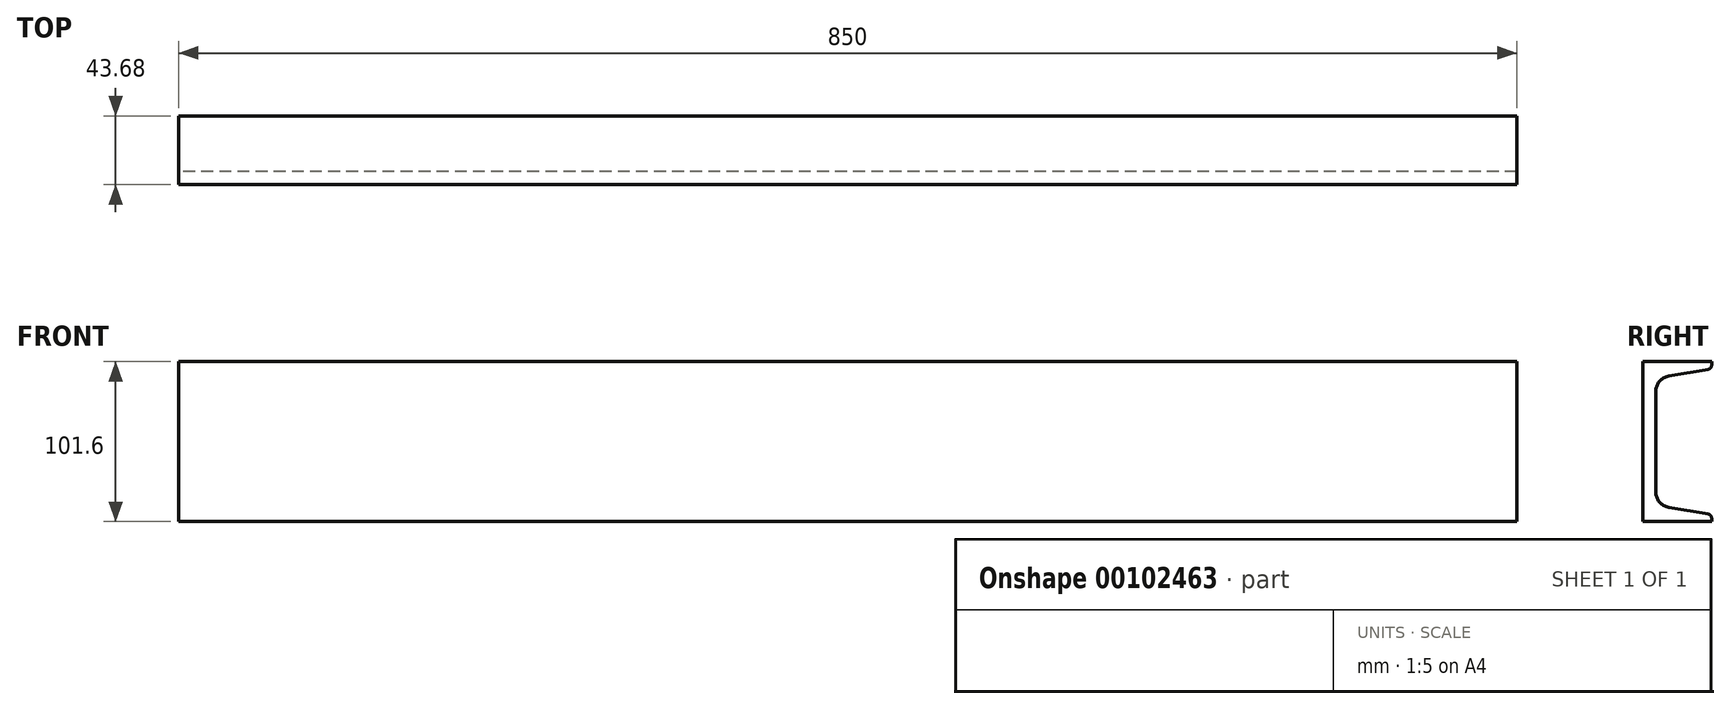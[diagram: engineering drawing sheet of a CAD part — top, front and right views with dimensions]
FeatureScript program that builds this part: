
annotation { "Feature Type Name" : "Feature", "Feature Type Description" : "" }
export const myFeature = defineFeature(function(context is Context, id is Id, definition is map)
    precondition{}
    {
        {
            var Q0;
            Q0=qCreatedBy(makeId("Right.planeOp"),FACE);
            var sketch = newSketch(context, id + "F0", { "sketchPlane" : qUnion([Q0])});
            skLineSegment(sketch, "E0", {"start": v(21.84, 50.8) * mm, "end": v(21.84, 48.6) * mm});
            skArc(sketch, "E1", {"start": v(21.84, 48.6) * mm, "mid": v(21.23, 46.93) * mm, "end": v(19.68, 46.03) * mm});
            skArc(sketch, "E2", {"start": v(-5.42, 41.6) * mm, "mid": v(-11.35, 38.18) * mm, "end": v(-13.7, 31.75) * mm, "construction": true});
            skArc(sketch, "E3", {"start": v(-13.7, -31.75) * mm, "mid": v(-11.35, -38.18) * mm, "end": v(-5.42, -41.6) * mm, "construction": true});
            skArc(sketch, "E4", {"start": v(19.68, -46.03) * mm, "mid": v(21.23, -46.93) * mm, "end": v(21.84, -48.6) * mm, "construction": true});
            skLineSegment(sketch, "E5", {"start": v(-21.84, 50.8) * mm, "end": v(21.84, 50.8) * mm});
            skLineSegment(sketch, "E6", {"start": v(-21.84, 50.8) * mm, "end": v(-21.84, -50.8) * mm});
            skLineSegment(sketch, "E7", {"start": v(-21.84, -50.8) * mm, "end": v(21.84, -50.8) * mm});
            skLineSegment(sketch, "E8", {"start": v(21.84, -50.8) * mm, "end": v(21.84, -48.6) * mm});
            skArc(sketch, "E9", {"start": v(21.84, -48.6) * mm, "mid": v(21.23, -46.93) * mm, "end": v(19.68, -46.03) * mm});
            skLineSegment(sketch, "E10", {"start": v(19.68, -46.03) * mm, "end": v(-5.42, -41.6) * mm});
            skArc(sketch, "E11", {"start": v(-5.42, -41.6) * mm, "mid": v(-11.35, -38.18) * mm, "end": v(-13.7, -31.75) * mm, "construction": true});
            skLineSegment(sketch, "E12", {"start": v(-13.7, -31.75) * mm, "end": v(-13.7, 31.75) * mm});
            skArc(sketch, "E13", {"start": v(-5.42, -41.6) * mm, "mid": v(-11.35, -38.18) * mm, "end": v(-13.7, -31.75) * mm});
            skArc(sketch, "E14", {"start": v(-13.7, 31.75) * mm, "mid": v(-11.35, 38.18) * mm, "end": v(-5.42, 41.6) * mm});
            skLineSegment(sketch, "E15", {"start": v(-5.42, 41.6) * mm, "end": v(19.68, 46.03) * mm});
            skSolve(sketch);
        }
        {
            var Q0;
            Q0=qSketchRegion(id+"F0",true);
            extrude(context, id + "F1", {"entities" : qUnion([Q0]), "depth" : 850 * mm});
        }
    });
